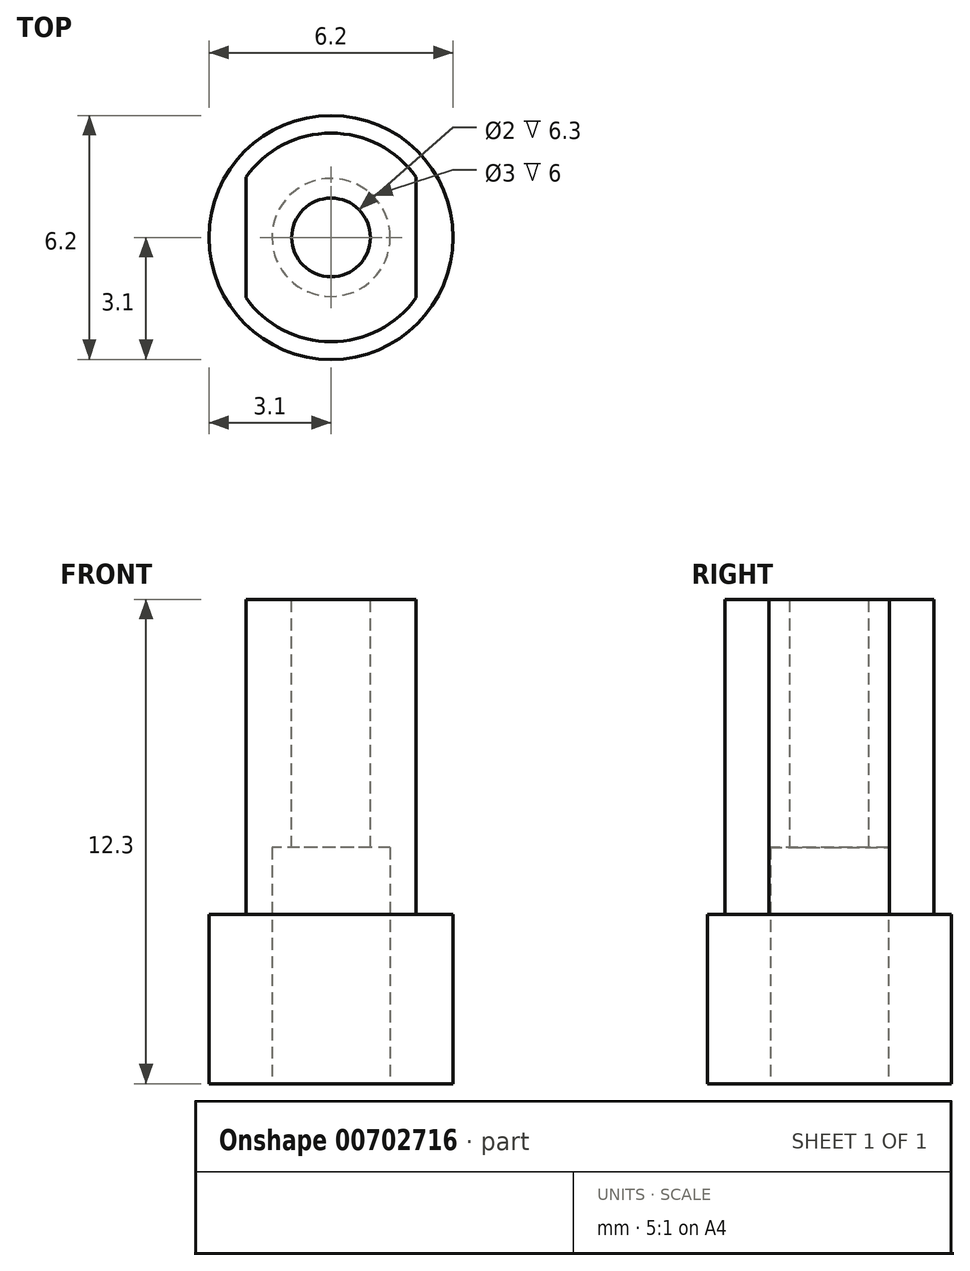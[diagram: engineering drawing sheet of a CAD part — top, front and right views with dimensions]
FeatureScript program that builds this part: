
annotation { "Feature Type Name" : "Feature", "Feature Type Description" : "" }
export const myFeature = defineFeature(function(context is Context, id is Id, definition is map)
    precondition{}
    {
        {
            var Q0;
            Q0=qCreatedBy(makeId("Top.planeOp"),FACE);
            var sketch = newSketch(context, id + "F0", { "sketchPlane" : qUnion([Q0])});
            skCircle(sketch, "E0", {"center": v(0, 0) * mm, "radius": 3.1 * mm});
            skCircle(sketch, "E1", {"center": v(0, 0) * mm, "radius": 1.5 * mm});
            skSolve(sketch);
        }
        {
            var Q0;
            Q0=makeQuery(id+"F0.imprint","IMPRINT",FACE,{"disambiguationData":[TD([[makeQuery(id+"F0.imprint","IMPRINT",EDGE,{"derivedFrom":sQuery(id+"F0.wireOp",EDGE,"E0")}),1.0]])]});
            var Q1;
            Q1=makeQuery(id+"F0.imprint","IMPRINT",FACE,{"disambiguationData":[TD([[makeQuery(id+"F0.imprint","IMPRINT",EDGE,{"derivedFrom":sQuery(id+"F0.wireOp",EDGE,"E1")}),1.0]])]});
            extrude(context, id + "F1", {"entities" : qUnion([Q0, Q1]), "depth" : 4.3 * mm, "offsetDistance" : 25.4 * mm});
        }
        {
            var Q0;
            Q0=makeQuery(id+"F1.opExtrude","CAP_FACE",FACE,{"disambiguationData":[OSD([sQuery(id+"F0.wireOp",EDGE,"E0")])],"isStart":false});
            var sketch = newSketch(context, id + "F2", { "sketchPlane" : qUnion([Q0])});
            skLineSegment(sketch, "E2.0", {"start": v(2.16, 1.53) * mm, "end": v(2.16, -1.53) * mm});
            skLineSegment(sketch, "E3.0", {"start": v(-2.16, 1.53) * mm, "end": v(-2.16, -1.53) * mm});
            skCircle(sketch, "E4", {"center": v(0, 0) * mm, "radius": 2.65 * mm});
            skSolve(sketch);
        }
        {
            var Q0;
            {var subQ0=sQuery(id+"F2.wireOp",EDGE,"E2.0");Q0=makeQuery(id+"F2.imprint","IMPRINT",FACE,{"disambiguationData":[TD([[makeQuery(id+"F2.imprint","IMPRINT",EDGE,{"derivedFrom":subQ0}),-1.0]])]});}
            extrude(context, id + "F3", {"entities" : qUnion([Q0]), "operationType" : NewBodyOperationType.ADD, "depth" : 8 * mm, "offsetDistance" : 25.4 * mm});
        }
        {
            var Q0;
            Q0=makeQuery(id+"F3.opExtrude","CAP_FACE",FACE,{"disambiguationData":[OSD([sQuery(id+"F0.wireOp",EDGE,"E0"),sQuery(id+"F2.wireOp",EDGE,"E2.0"),sQuery(id+"F2.wireOp",EDGE,"E3.0")])],"isStart":false});
            var sketch = newSketch(context, id + "F4", { "sketchPlane" : qUnion([Q0])});
            skCircle(sketch, "E5", {"center": v(0, 0) * mm, "radius": 1 * mm});
            skSolve(sketch);
        }
        {
            var Q0;
            Q0=makeQuery(id+"F4.imprint","IMPRINT",FACE,{"disambiguationData":[TD([[makeQuery(id+"F4.imprint","IMPRINT",EDGE,{"derivedFrom":sQuery(id+"F4.wireOp",EDGE,"E5")}),1.0]])]});
            extrude(context, id + "F5", {"entities" : qUnion([Q0]), "operationType" : NewBodyOperationType.REMOVE, "oppositeDirection" : true, "depth" : 8 * mm, "offsetDistance" : 25.4 * mm});
        }
        {
            var Q0;
            Q0=makeQuery(id+"F0.imprint","IMPRINT",FACE,{"disambiguationData":[TD([[makeQuery(id+"F0.imprint","IMPRINT",EDGE,{"derivedFrom":sQuery(id+"F0.wireOp",EDGE,"E1")}),1.0]])]});
            extrude(context, id + "F6", {"entities" : qUnion([Q0]), "operationType" : NewBodyOperationType.REMOVE, "depth" : 6 * mm, "offsetDistance" : 25.4 * mm});
        }
    });
